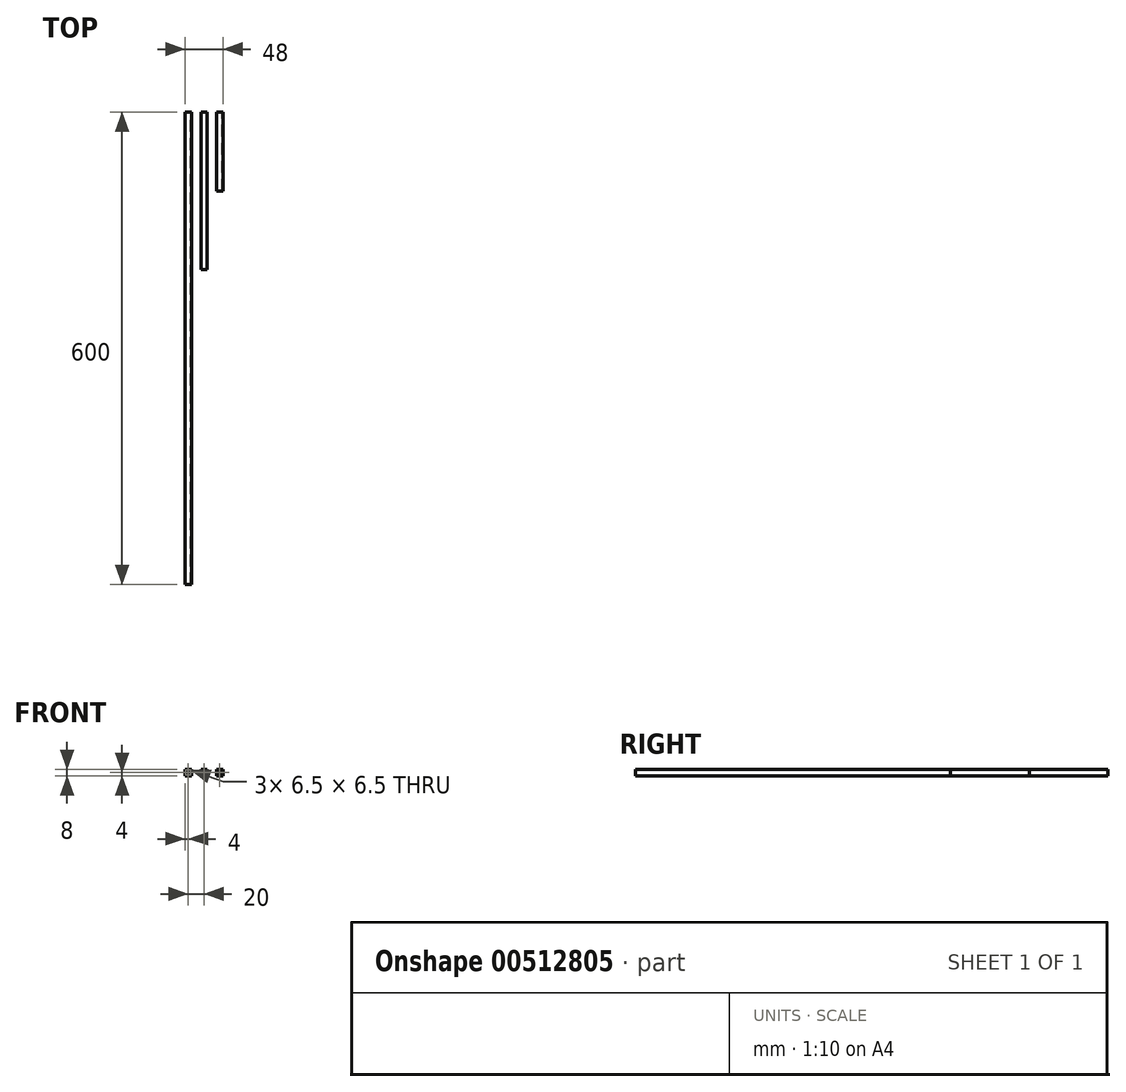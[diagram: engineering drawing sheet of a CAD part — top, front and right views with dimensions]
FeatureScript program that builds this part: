
annotation { "Feature Type Name" : "Feature", "Feature Type Description" : "" }
export const myFeature = defineFeature(function(context is Context, id is Id, definition is map)
    precondition{}
    {
        {
            var Q0;
            Q0=qCreatedBy(makeId("Front.planeOp"),FACE);
            var sketch = newSketch(context, id + "F0", { "sketchPlane" : qUnion([Q0])});
            skLineSegment(sketch, "E0.bottom", {"start": v(4, 4) * mm, "end": v(-4, 4) * mm});
            skLineSegment(sketch, "E0.top", {"start": v(4, -4) * mm, "end": v(-4, -4) * mm});
            skLineSegment(sketch, "E0.left", {"start": v(4, 4) * mm, "end": v(4, -4) * mm});
            skLineSegment(sketch, "E0.right", {"start": v(-4, 4) * mm, "end": v(-4, -4) * mm});
            skPoint(sketch, "E0.middle", {"position": v(0, 0) * mm});
            skLineSegment(sketch, "E1.bottom", {"start": v(3.25, 3.25) * mm, "end": v(-3.25, 3.25) * mm});
            skLineSegment(sketch, "E1.top", {"start": v(3.25, -3.25) * mm, "end": v(-3.25, -3.25) * mm});
            skLineSegment(sketch, "E1.left", {"start": v(3.25, 3.25) * mm, "end": v(3.25, -3.25) * mm});
            skLineSegment(sketch, "E1.right", {"start": v(-3.25, 3.25) * mm, "end": v(-3.25, -3.25) * mm});
            skSolve(sketch);
        }
        {
            var Q0;
            Q0 = qSketchRegion(id + "F0", true);
            extrude(context, id + "F1", {"entities" : qUnion([Q0]), "depth" : 600 * mm});
        }
        {
            var Q0;
            Q0=qCreatedBy(makeId("Front.planeOp"),FACE);
            var sketch = newSketch(context, id + "F2", { "sketchPlane" : qUnion([Q0])});
            skPoint(sketch, "E2", {"position": v(20, 0) * mm});
            skLineSegment(sketch, "E3.bottom", {"start": v(24, 4) * mm, "end": v(16, 4) * mm});
            skLineSegment(sketch, "E3.top", {"start": v(24, -4) * mm, "end": v(16, -4) * mm});
            skLineSegment(sketch, "E3.left", {"start": v(24, 4) * mm, "end": v(24, -4) * mm});
            skLineSegment(sketch, "E3.right", {"start": v(16, 4) * mm, "end": v(16, -4) * mm});
            skLineSegment(sketch, "E4.bottom", {"start": v(23.25, 3.25) * mm, "end": v(16.75, 3.25) * mm});
            skLineSegment(sketch, "E4.top", {"start": v(23.25, -3.25) * mm, "end": v(16.75, -3.25) * mm});
            skLineSegment(sketch, "E4.left", {"start": v(23.25, 3.25) * mm, "end": v(23.25, -3.25) * mm});
            skLineSegment(sketch, "E4.right", {"start": v(16.75, 3.25) * mm, "end": v(16.75, -3.25) * mm});
            skSolve(sketch);
        }
        {
            var Q0;
            Q0 = qSketchRegion(id + "F2", true);
            extrude(context, id + "F3", {"entities" : qUnion([Q0]), "depth" : 200 * mm});
        }
        {
            var Q0;
            Q0=qCreatedBy(makeId("Front.planeOp"),FACE);
            var sketch = newSketch(context, id + "F4", { "sketchPlane" : qUnion([Q0])});
            skPoint(sketch, "E5", {"position": v(40, 0) * mm});
            skLineSegment(sketch, "E6.bottom", {"start": v(44, 4) * mm, "end": v(36, 4) * mm});
            skLineSegment(sketch, "E6.top", {"start": v(44, -4) * mm, "end": v(36, -4) * mm});
            skLineSegment(sketch, "E6.left", {"start": v(44, 4) * mm, "end": v(44, -4) * mm});
            skLineSegment(sketch, "E6.right", {"start": v(36, 4) * mm, "end": v(36, -4) * mm});
            skLineSegment(sketch, "E7.bottom", {"start": v(43.25, 3.25) * mm, "end": v(36.75, 3.25) * mm});
            skLineSegment(sketch, "E7.top", {"start": v(43.25, -3.25) * mm, "end": v(36.75, -3.25) * mm});
            skLineSegment(sketch, "E7.left", {"start": v(43.25, 3.25) * mm, "end": v(43.25, -3.25) * mm});
            skLineSegment(sketch, "E7.right", {"start": v(36.75, 3.25) * mm, "end": v(36.75, -3.25) * mm});
            skSolve(sketch);
        }
        {
            var Q0;
            Q0 = qSketchRegion(id + "F4", true);
            extrude(context, id + "F5", {"entities" : qUnion([Q0]), "depth" : 100 * mm});
        }
    });
